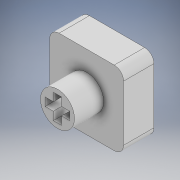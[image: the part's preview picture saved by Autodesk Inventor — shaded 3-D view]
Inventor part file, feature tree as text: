
AUTODESK INVENTOR PART (.ipt)
format: ipt  version: 2022 (Build 260153000, 153)  size: 212,992 bytes
history: native  units: in
note: dims shown in document units (in); Inventor stores cm internally (conversion verified against a paired STEP export)
features: sketch x4, extrude x3, plane x1, projected_geometry x1
ambient origin geometry x8: Origin, YZ Plane, XZ Plane, XY Plane, X Axis, Y Axis, Z Axis, Center Point
bodies: Body1 (feature_tree)
feature tree (9):
  sketch  "Sketch1"  dims[d3=0.2205in d4=0.1594in]
  plane  "Work Plane1"
  sketch  "Sketch2"  dims[d5=0.0531in d6=0.1594in]
  extrude  "Extrusion3"  Depth=0.1594in
  extrude  "Extrusion4"  Depth=0.1594in
  extrude  "Extrusion5"  Depth=0.5016in
  projected_geometry  "Projected Loop1"
  sketch  "Sketch3"  dims[d7=0.0531in d10=0.5016in]
  sketch  "Sketch4"  dims[d12=0.1969in d13=0.0in d14=0.2205in d15=0.1594in d16=0.0531in d17=0.1594in d18=0.0531in d19=0.189in d20=0.0in d21=0.0892in d22=0.2693in d23=0.0354in d24=0.0in]
